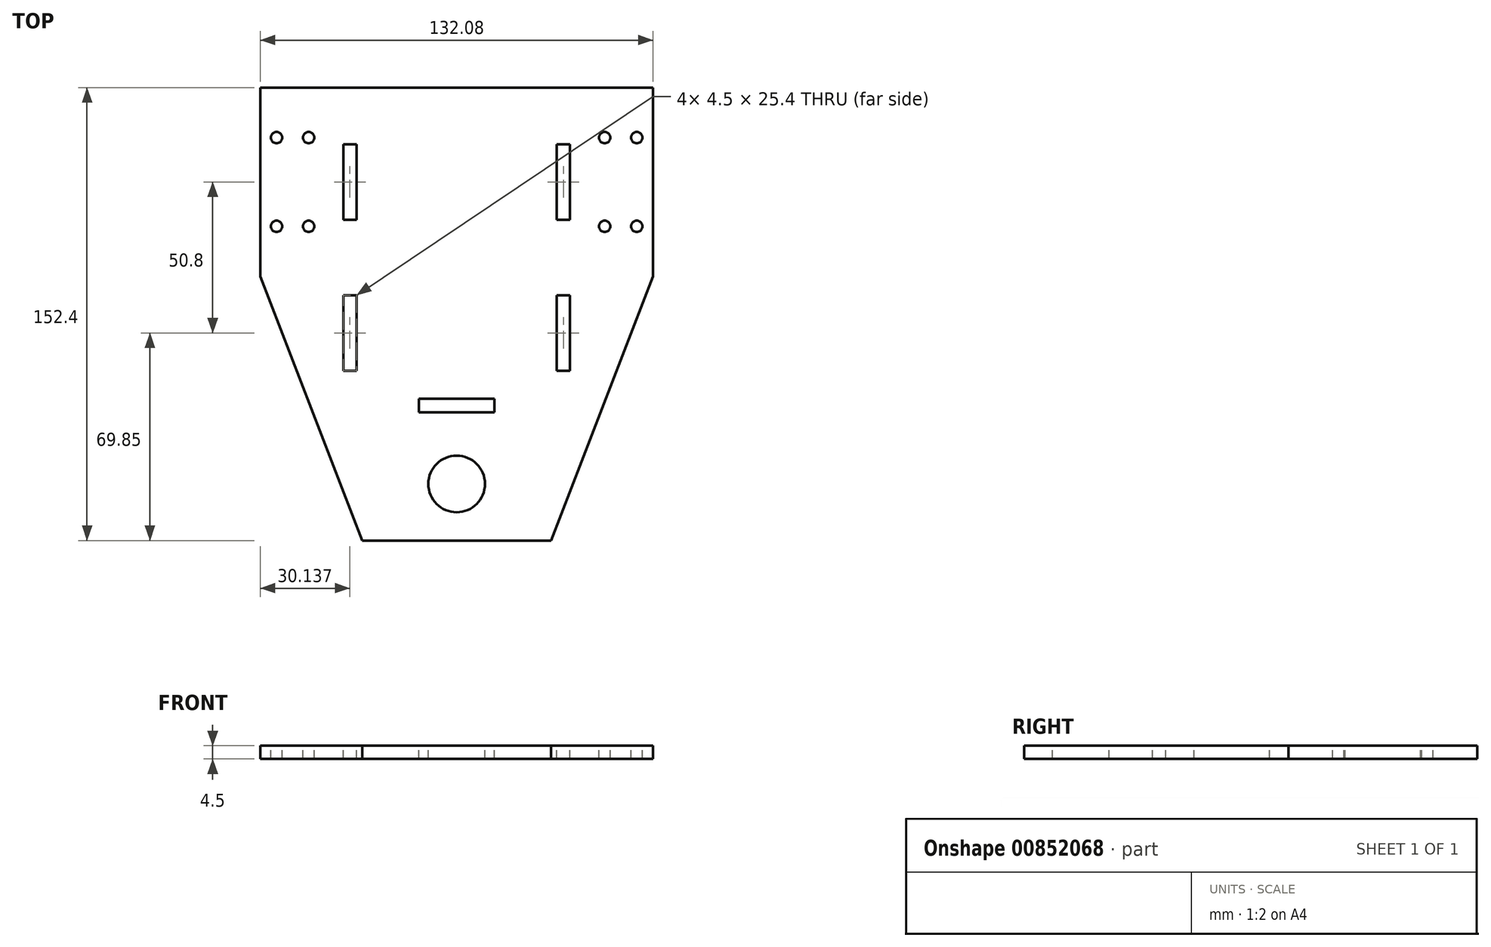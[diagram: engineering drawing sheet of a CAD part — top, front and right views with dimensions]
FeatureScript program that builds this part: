
annotation { "Feature Type Name" : "Feature", "Feature Type Description" : "" }
export const myFeature = defineFeature(function(context is Context, id is Id, definition is map)
    precondition{}
    {
        {
            var Q0;
            Q0=qCreatedBy(makeId("Top.planeOp"),FACE);
            var sketch = newSketch(context, id + "F0", { "sketchPlane" : qUnion([Q0])});
            skLineSegment(sketch, "E0", {"start": v(-66.04, 76.2) * mm, "end": v(66.04, 76.2) * mm});
            skLineSegment(sketch, "E1", {"start": v(66.04, 76.2) * mm, "end": v(66.04, 12.7) * mm});
            skLineSegment(sketch, "E2", {"start": v(66.04, 12.7) * mm, "end": v(31.75, -76.2) * mm});
            skLineSegment(sketch, "E3", {"start": v(31.75, -76.2) * mm, "end": v(-31.75, -76.2) * mm});
            skLineSegment(sketch, "E4", {"start": v(-31.75, -76.2) * mm, "end": v(-66.04, 12.7) * mm});
            skLineSegment(sketch, "E5", {"start": v(-66.04, 12.7) * mm, "end": v(-66.04, 76.2) * mm});
            skLineSegment(sketch, "E6", {"start": v(0, 76.2) * mm, "end": v(0, -76.2) * mm, "construction": true});
            skSolve(sketch);
        }
        {
            var Q0;
            Q0 = qSketchRegion(id + "F0", true);
            extrude(context, id + "F1", {"entities" : qUnion([Q0]), "depth" : 4.5 * mm, "offsetDistance" : 25.4 * mm});
        }
        {
            var Q0;
            Q0=makeQuery(id+"F1.opExtrude","CAP_FACE",FACE,{"disambiguationData":[OSD([sQuery(id+"F0.wireOp",EDGE,"E0"),sQuery(id+"F0.wireOp",EDGE,"E1"),sQuery(id+"F0.wireOp",EDGE,"E2"),sQuery(id+"F0.wireOp",EDGE,"E3"),sQuery(id+"F0.wireOp",EDGE,"E4"),sQuery(id+"F0.wireOp",EDGE,"E5")])],"isStart":false});
            var sketch = newSketch(context, id + "F2", { "sketchPlane" : qUnion([Q0])});
            skLineSegment(sketch, "E7.bottom", {"start": v(-60.58, 59.37) * mm, "end": v(-49.78, 59.37) * mm, "construction": true});
            skLineSegment(sketch, "E7.top", {"start": v(-60.58, 29.53) * mm, "end": v(-49.78, 29.53) * mm, "construction": true});
            skLineSegment(sketch, "E7.left", {"start": v(-60.58, 59.37) * mm, "end": v(-60.58, 29.53) * mm, "construction": true});
            skLineSegment(sketch, "E7.right", {"start": v(-49.78, 59.37) * mm, "end": v(-49.78, 29.53) * mm, "construction": true});
            skLineSegment(sketch, "E8", {"start": v(0, 76.2) * mm, "end": v(0, 0) * mm, "construction": true});
            skCircle(sketch, "E9", {"center": v(-60.58, 59.37) * mm, "radius": 1.9 * mm});
            skCircle(sketch, "E10", {"center": v(-49.78, 59.37) * mm, "radius": 1.9 * mm});
            skCircle(sketch, "E11", {"center": v(-49.78, 29.53) * mm, "radius": 1.9 * mm});
            skCircle(sketch, "E12", {"center": v(-60.58, 29.53) * mm, "radius": 1.9 * mm});
            skLineSegment(sketch, "E13", {"start": v(-66.04, 44.45) * mm, "end": v(-49.78, 44.45) * mm, "construction": true});
            skCircle(sketch, "E14.MirrorC", {"center": v(60.58, 59.37) * mm, "radius": 1.9 * mm});
            skLineSegment(sketch, "E15.MirrorCS", {"start": v(60.58, 59.37) * mm, "end": v(49.78, 59.37) * mm, "construction": true});
            skLineSegment(sketch, "E16.MirrorCS", {"start": v(49.78, 59.37) * mm, "end": v(49.78, 29.53) * mm, "construction": true});
            skLineSegment(sketch, "E17.MirrorCS", {"start": v(60.58, 59.37) * mm, "end": v(60.58, 29.53) * mm, "construction": true});
            skCircle(sketch, "E18.MirrorC", {"center": v(49.78, 29.53) * mm, "radius": 1.9 * mm});
            skLineSegment(sketch, "E19.MirrorCS", {"start": v(60.58, 29.53) * mm, "end": v(49.78, 29.53) * mm, "construction": true});
            skLineSegment(sketch, "E20.MirrorCS", {"start": v(66.04, 44.45) * mm, "end": v(49.78, 44.45) * mm, "construction": true});
            skCircle(sketch, "E21.MirrorC", {"center": v(49.78, 59.37) * mm, "radius": 1.9 * mm});
            skCircle(sketch, "E22.MirrorC", {"center": v(60.58, 29.53) * mm, "radius": 1.9 * mm});
            skSolve(sketch);
        }
        {
            var Q0;
            Q0 = qSketchRegion(id + "F2", true);
            extrude(context, id + "F3", {"entities" : qUnion([Q0]), "operationType" : NewBodyOperationType.REMOVE, "endBound" : BoundingType.THROUGH_ALL, "oppositeDirection" : true, "depth" : 25.4 * mm, "offsetDistance" : 25.4 * mm});
        }
        {
            var Q0;
            Q0=makeQuery(id+"F1.opExtrude","CAP_FACE",FACE,{"disambiguationData":[OSD([sQuery(id+"F0.wireOp",EDGE,"E0"),sQuery(id+"F0.wireOp",EDGE,"E1"),sQuery(id+"F0.wireOp",EDGE,"E2"),sQuery(id+"F0.wireOp",EDGE,"E3"),sQuery(id+"F0.wireOp",EDGE,"E4"),sQuery(id+"F0.wireOp",EDGE,"E5")])],"isStart":false});
            var sketch = newSketch(context, id + "F4", { "sketchPlane" : qUnion([Q0])});
            skLineSegment(sketch, "E23.bottom", {"start": v(-33.65, 76.2) * mm, "end": v(33.65, 76.2) * mm, "construction": true});
            skLineSegment(sketch, "E23.top", {"start": v(-33.65, -38.1) * mm, "end": v(33.65, -38.1) * mm, "construction": true});
            skLineSegment(sketch, "E23.left", {"start": v(-33.65, 76.2) * mm, "end": v(-33.65, -38.1) * mm, "construction": true});
            skLineSegment(sketch, "E23.right", {"start": v(33.65, 76.2) * mm, "end": v(33.65, -38.1) * mm, "construction": true});
            skLineSegment(sketch, "E24", {"start": v(0, 76.2) * mm, "end": v(0, -38.1) * mm, "construction": true});
            skLineSegment(sketch, "E25.bottom", {"start": v(-38.15, 57.15) * mm, "end": v(-33.65, 57.15) * mm});
            skLineSegment(sketch, "E25.top", {"start": v(-38.15, 31.75) * mm, "end": v(-33.65, 31.75) * mm});
            skLineSegment(sketch, "E25.left", {"start": v(-38.15, 57.15) * mm, "end": v(-38.15, 31.75) * mm});
            skLineSegment(sketch, "E25.right", {"start": v(-33.65, 57.15) * mm, "end": v(-33.65, 31.75) * mm});
            skLineSegment(sketch, "E26", {"start": v(-33.65, 19.05) * mm, "end": v(33.65, 19.05) * mm, "construction": true});
            skLineSegment(sketch, "E27.MirrorCS", {"start": v(-38.15, -19.05) * mm, "end": v(-38.15, 6.35) * mm});
            skLineSegment(sketch, "E28.MirrorCS", {"start": v(-38.15, -19.05) * mm, "end": v(-33.65, -19.05) * mm});
            skLineSegment(sketch, "E29.MirrorCS", {"start": v(-38.15, 6.35) * mm, "end": v(-33.65, 6.35) * mm});
            skLineSegment(sketch, "E30.MirrorCS", {"start": v(-33.65, -19.05) * mm, "end": v(-33.65, 6.35) * mm});
            skLineSegment(sketch, "E31.MirrorCS", {"start": v(38.15, 31.75) * mm, "end": v(33.65, 31.75) * mm});
            skLineSegment(sketch, "E32.MirrorCS", {"start": v(38.15, -19.05) * mm, "end": v(33.65, -19.05) * mm});
            skLineSegment(sketch, "E33.MirrorCS", {"start": v(38.15, 57.15) * mm, "end": v(33.65, 57.15) * mm});
            skLineSegment(sketch, "E34.MirrorCS", {"start": v(38.15, 6.35) * mm, "end": v(33.65, 6.35) * mm});
            skLineSegment(sketch, "E35.MirrorCS", {"start": v(38.15, -19.05) * mm, "end": v(38.15, 6.35) * mm});
            skLineSegment(sketch, "E36.MirrorCS", {"start": v(38.15, 57.15) * mm, "end": v(38.15, 31.75) * mm});
            skLineSegment(sketch, "E37.MirrorCS", {"start": v(33.65, -19.05) * mm, "end": v(33.65, 6.35) * mm});
            skLineSegment(sketch, "E38.MirrorCS", {"start": v(33.65, 57.15) * mm, "end": v(33.65, 31.75) * mm});
            skCircle(sketch, "E39", {"center": v(0, -57.15) * mm, "radius": 9.53 * mm});
            skLineSegment(sketch, "E40.bottom", {"start": v(-12.7, -28.52) * mm, "end": v(12.7, -28.52) * mm});
            skLineSegment(sketch, "E40.top", {"start": v(-12.7, -33.02) * mm, "end": v(12.7, -33.02) * mm});
            skLineSegment(sketch, "E40.left", {"start": v(-12.7, -28.52) * mm, "end": v(-12.7, -33.02) * mm});
            skLineSegment(sketch, "E40.right", {"start": v(12.7, -28.52) * mm, "end": v(12.7, -33.02) * mm});
            skLineSegment(sketch, "E41", {"start": v(-12.7, -33.02) * mm, "end": v(0, 76.2) * mm, "construction": true});
            skLineSegment(sketch, "E42", {"start": v(0, 76.2) * mm, "end": v(12.7, -33.02) * mm, "construction": true});
            skSolve(sketch);
        }
        {
            var Q0;
            Q0 = qSketchRegion(id + "F4", true);
            extrude(context, id + "F5", {"entities" : qUnion([Q0]), "operationType" : NewBodyOperationType.REMOVE, "endBound" : BoundingType.THROUGH_ALL, "oppositeDirection" : true, "depth" : 25.4 * mm, "offsetDistance" : 25.4 * mm});
        }
    });
